# Revit family: OWP OPTIMA LED
name_source: partatom
category: Осветительные приборы
revit_build: Autodesk Revit 2016 (Build: 20150220_1215(x64)
units: mm (PartAtom-declared; Revit-internal decimal feet)

## family parameters
Источник света = Да
Общий = Нет
Основа = Грань
При загрузке вырезать с полостями = Нет
Размер круглого соединителя = Использовать диаметр
Тип детали = Нормальный
Точка расчета площади = Нет

## types (1)
- OWP OPTIMA LED
    ADSK_Единица измерения = Шт.
    ADSK_Завод-изготовитель = ООО МГК Световые технологии
    ADSK_Количество фаз = 1
    ADSK_Количество фаз числовое = 1
    ADSK_Коэффициент мощности = 0.98
    ADSK_Масса = 8.5
    ADSK_Наименование = Оптимизированная по цене версия светильника OWP ECO LED, за счет применения линейных светодиодных модулей. Не имеет выступающих элементов и винтов, создающих условия для скопления пыли. Поверхность светильника устойчива для обработки дезинфицирующими жидкостями. Светильники удовлетворяют требованиям для применения в образовательных учреждениях. Значение габаритной яркости для модификаций с опаловым рассеивателем из ПММА составляет 3400 кд/м. кв., неравномерность распеделения яркости составялет не более 2:1
    ADSK_Напряжение = 230 В
    ADSK_Номинальная мощность = 0 кВт
    ADSK_Полная мощность = 0 кВ·А
    ADSK_Размер_Длина = 595 мм
    ADSK_Размер_Ширина = 595 мм
    ADSK_Ток = 0 А
    ADSK_Энергоэффективность = 0 лм/Вт
    IP Class = IP54
    URL = https://ltcompany.com
    Блок аварийного питания = Нет
    Видимая форма излучения при визуализации = Нет
    Группа модели = Светильники
    Длина_свет = 565 мм
    Изготовитель = ООО МГК Световые технологии
    Излучение по длине прямоугольника = 595 мм
    Излучение по ширине прямоугольника = 595 мм
    Класс Защиты = I
    Класс пожароопасности = П-II, IIа
    Климатическая зона = УХЛ2
    Код по классификатору = D5020200
    Корпус = Белый металл
    Область использования = Медицинские учреждения, Промышленные предприятия, Чистые помещения
    Описание = Оптимизированная по цене версия светильника OWP ECO LED, за счет применения линейных светодиодных модулей. Не имеет выступающих элементов и винтов, создающих условия для скопления пыли. Поверхность светильника устойчива для обработки дезинфицирующими жидкостями. Светильники удовлетворяют требованиям для применения в образовательных учреждениях. Значение габаритной яркости для модификаций с опаловым рассеивателем из ПММА составляет 3400 кд/м. кв., неравномерность распеделения яркости составялет не более 2:1
    Отметка по умолчанию = 0 мм
    Плафон = Плафон самосвечение
    Полная установленная мощность = 0 кВ·А
    Разработчик = ООО ПРОРУБИМ
    Разработчик (телефон) = +7 (495) 649-85-43
    Светофильтр = 16777215
    Смещение цветовой температуры при затухании лампы = <Нет>
    Тип ИС = LED
    Тип продукции = Светильники
    Угол наклона = -90.00°
    Файл фотометрической сетки = generic
    Ширина_свет = 565 мм
